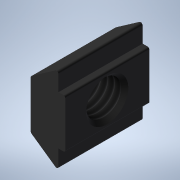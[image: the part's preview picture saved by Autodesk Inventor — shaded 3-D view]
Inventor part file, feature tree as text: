
AUTODESK INVENTOR PART (.ipt)
format: ipt  version: 2021 (Build 250183000, 183)  size: 150,528 bytes
history: native  units: mm
features: other x28, sketch x2, extrude x1, revolve x1, thread x1
ambient origin geometry x8: Origin, YZ Plane, XZ Plane, XY Plane, X Axis, Y Axis, Z Axis, Center Point
bodies: Solid1 (feature_tree)
feature tree (33):
  extrude  "Extrusion1"  TaperAngle=360.0deg  [1 undecoded]
  revolve  "Revolution1"  [1 undecoded]
  thread  "Thread1"  [1 undecoded]
  other  "nut_XY"
  other  "nut_YZ"
  other  "nut_ZX"
  other  "nut_X"
  other  "nut_Y"
  other  "nut_Z"
  other  "nut_Center"
  other  "to_bolt_XY"
  other  "to_bolt_YZ"
  other  "to_bolt_ZX"
  other  "to_bolt_X"
  other  "to_bolt_Y"
  other  "to_bolt_Z"
  other  "to_bolt_Center"
  other  "to_frames_XY"
  other  "to_frames_YZ"
  other  "to_frames_ZX"
  other  "to_frames_X"
  other  "to_frames_Y"
  other  "to_frames_Z"
  other  "to_frames_Center"
  other  "to_lane_XY"
  other  "to_lane_YZ"
  other  "to_lane_ZX"
  other  "to_lane_X"
  other  "to_lane_Y"
  other  "to_lane_Z"
  other  "to_lane_Center"
  sketch  "Sketch_2"  dims[d0=10.0mm d1=0.0mm d2=360.0deg]
  sketch  "Sketch_5"  dims[d3=3.234mm d4=0.0mm d5=0.0mm d6=0.0mm]
note: 3 required parameter values undecoded (feature->parameter linkage not recoverable at this tier; creation-order binding heuristic only, values carry confidence <= 0.55)